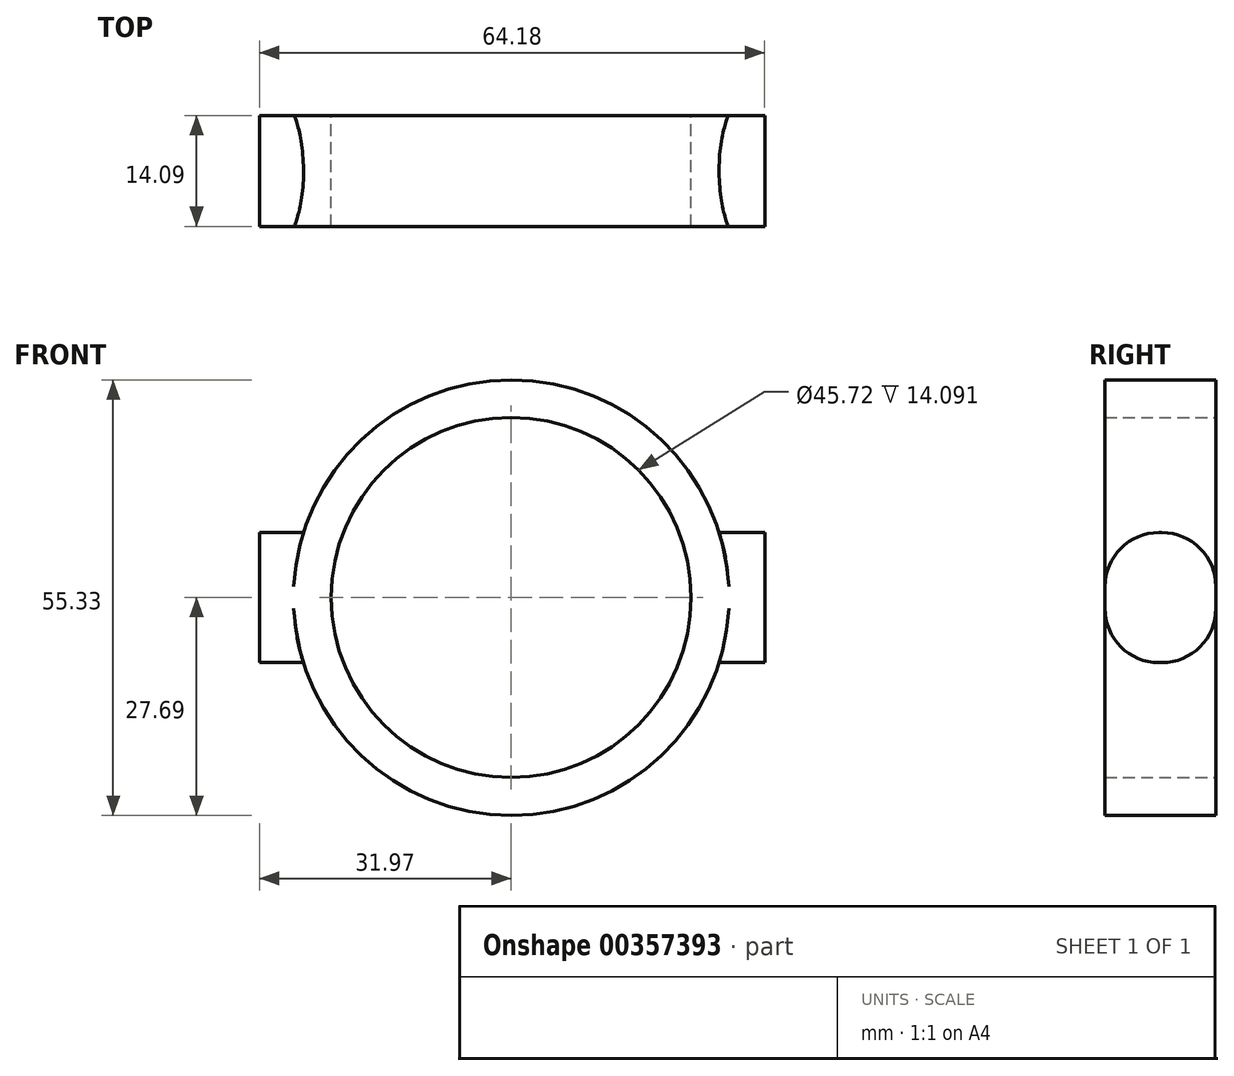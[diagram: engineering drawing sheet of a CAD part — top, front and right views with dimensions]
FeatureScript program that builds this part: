
annotation { "Feature Type Name" : "Feature", "Feature Type Description" : "" }
export const myFeature = defineFeature(function(context is Context, id is Id, definition is map)
    precondition{}
    {
        {
            var Q0;
            Q0=qCreatedBy(makeId("Front.planeOp"),FACE);
            var sketch = newSketch(context, id + "F0", { "sketchPlane" : qUnion([Q0])});
            skCircle(sketch, "E0", {"center": v(0.02, -0.03) * mm, "radius": 27.66 * mm});
            skPoint(sketch, "E0.first.point", {"position": v(27.68, 0) * mm});
            skPoint(sketch, "E0.second.point", {"position": v(-27.65, 0) * mm});
            skPoint(sketch, "E0.third.point", {"position": v(0, -27.7) * mm});
            skLineSegment(sketch, "E1", {"start": v(32.21, 8.25) * mm, "end": v(-31.97, 8.25) * mm});
            skLineSegment(sketch, "E2", {"start": v(-31.97, -8.28) * mm, "end": v(32.21, -8.28) * mm});
            skLineSegment(sketch, "E3", {"start": v(-31.97, 8.25) * mm, "end": v(-31.97, -8.28) * mm});
            skLineSegment(sketch, "E4", {"start": v(32.21, 8.25) * mm, "end": v(32.21, -8.28) * mm});
            skSolve(sketch);
        }
        {
            var Q0;
            Q0=qSketchRegion(id+"F0",true);
            var Q1;
            Q1=sQuery(id+"F0.wireOp",EDGE,"E0");
            var Q2;
            Q2=sQuery(id+"F0.wireOp",EDGE,"E2");
            var Q3;
            Q3=sQuery(id+"F0.wireOp",EDGE,"E1");
            var Q4;
            Q4=sQuery(id+"F0.wireOp",EDGE,"E3");
            var Q5;
            Q5=sQuery(id+"F0.wireOp",EDGE,"E4");
            extrude(context, id + "F1", {"entities" : qUnion([Q0]), "surfaceEntities" : qUnion([Q1, Q2, Q3, Q4, Q5]), "depth" : 14.1 * mm});
        }
        {
            var Q0;
            Q0=qCreatedBy(makeId("Front.planeOp"),FACE);
            var sketch = newSketch(context, id + "F2", { "sketchPlane" : qUnion([Q0])});
            skPoint(sketch, "E5", {"position": v(0, 0) * mm});
            skSolve(sketch);
        }
        {
            var Q0;
            Q0=sQuery(id+"F2.wireOp",VERTEX,"E5");
            var Q1;
            Q1=makeQuery(id+"F1.opExtrude","SWEPT_BODY",BODY,{"disambiguationData":[OSD([sQuery(id+"F0.wireOp",EDGE,"E0"),sQuery(id+"F0.wireOp",EDGE,"E1"),sQuery(id+"F0.wireOp",EDGE,"E2"),sQuery(id+"F0.wireOp",EDGE,"E3"),sQuery(id+"F0.wireOp",EDGE,"E4")])]});
            hole(context, id + "F3", {"style" : HoleStyle.SIMPLE, "endStyle" : HoleEndStyle.THROUGH, "oppositeDirection" : true, "holeDiameter" : 45.72 * mm, "isTappedThrough" : true, "tappedDepth" : 12.7 * mm, "tapClearance" : 3, "locations" : qUnion([Q0]), "scope" : qUnion([Q1])});
        }
        {
            var Q0;
            {var subQ0=sQuery(id+"F0.wireOp",EDGE,"E2");Q0=makeQuery(id+"F1.opExtrude","CAP_EDGE",EDGE,{"disambiguationData":[OSD([subQ0]),TDD([makeQuery(id+"F0.imprint","IMPRINT",EDGE,{"disambiguationData":[TD([[makeQuery(id+"F0.imprint","INTERSECT",VERTEX,{"derivedFrom":[subQ0,sQuery(id+"F0.wireOp",EDGE,"E4")]}),1.0]])],"derivedFrom":subQ0})])],"isStart":false});}
            var Q1;
            {var subQ0=sQuery(id+"F0.wireOp",EDGE,"E2");Q1=makeQuery(id+"F1.opExtrude","CAP_EDGE",EDGE,{"disambiguationData":[OSD([subQ0]),TDD([makeQuery(id+"F0.imprint","IMPRINT",EDGE,{"disambiguationData":[TD([[makeQuery(id+"F0.imprint","INTERSECT",VERTEX,{"derivedFrom":[subQ0,sQuery(id+"F0.wireOp",EDGE,"E4")]}),1.0]])],"derivedFrom":subQ0})])],"isStart":true});}
            var Q2;
            {var subQ0=sQuery(id+"F0.wireOp",EDGE,"E1");Q2=makeQuery(id+"F1.opExtrude","CAP_EDGE",EDGE,{"disambiguationData":[OSD([subQ0]),TDD([makeQuery(id+"F0.imprint","IMPRINT",EDGE,{"disambiguationData":[TD([[makeQuery(id+"F0.imprint","INTERSECT",VERTEX,{"derivedFrom":[subQ0,sQuery(id+"F0.wireOp",EDGE,"E4")]}),-1.0]])],"derivedFrom":subQ0})])],"isStart":false});}
            var Q3;
            {var subQ0=sQuery(id+"F0.wireOp",EDGE,"E1");Q3=makeQuery(id+"F1.opExtrude","CAP_EDGE",EDGE,{"disambiguationData":[OSD([subQ0]),TDD([makeQuery(id+"F0.imprint","IMPRINT",EDGE,{"disambiguationData":[TD([[makeQuery(id+"F0.imprint","INTERSECT",VERTEX,{"derivedFrom":[subQ0,sQuery(id+"F0.wireOp",EDGE,"E4")]}),-1.0]])],"derivedFrom":subQ0})])],"isStart":true});}
            fillet(context, id + "F4", {"entities" : qUnion([Q0, Q1, Q2, Q3]), "radius" : 6.86 * mm, "tangentPropagation" : true, "allowEdgeOverflow" : false});
        }
        {
            var Q0;
            {var subQ0=sQuery(id+"F0.wireOp",EDGE,"E2");Q0=makeQuery(id+"F1.opExtrude","CAP_EDGE",EDGE,{"disambiguationData":[OSD([subQ0]),TDD([makeQuery(id+"F0.imprint","IMPRINT",EDGE,{"disambiguationData":[TD([[makeQuery(id+"F0.imprint","INTERSECT",VERTEX,{"derivedFrom":[subQ0,sQuery(id+"F0.wireOp",EDGE,"E3")]}),-1.0]])],"derivedFrom":subQ0})])],"isStart":false});}
            var Q1;
            {var subQ0=sQuery(id+"F0.wireOp",EDGE,"E1");Q1=makeQuery(id+"F1.opExtrude","CAP_EDGE",EDGE,{"disambiguationData":[OSD([subQ0]),TDD([makeQuery(id+"F0.imprint","IMPRINT",EDGE,{"disambiguationData":[TD([[makeQuery(id+"F0.imprint","INTERSECT",VERTEX,{"derivedFrom":[subQ0,sQuery(id+"F0.wireOp",EDGE,"E3")]}),1.0]])],"derivedFrom":subQ0})])],"isStart":false});}
            var Q2;
            {var subQ0=sQuery(id+"F0.wireOp",EDGE,"E1");Q2=makeQuery(id+"F1.opExtrude","CAP_EDGE",EDGE,{"disambiguationData":[OSD([subQ0]),TDD([makeQuery(id+"F0.imprint","IMPRINT",EDGE,{"disambiguationData":[TD([[makeQuery(id+"F0.imprint","INTERSECT",VERTEX,{"derivedFrom":[subQ0,sQuery(id+"F0.wireOp",EDGE,"E3")]}),1.0]])],"derivedFrom":subQ0})])],"isStart":true});}
            var Q3;
            {var subQ0=sQuery(id+"F0.wireOp",EDGE,"E2");Q3=makeQuery(id+"F1.opExtrude","CAP_EDGE",EDGE,{"disambiguationData":[OSD([subQ0]),TDD([makeQuery(id+"F0.imprint","IMPRINT",EDGE,{"disambiguationData":[TD([[makeQuery(id+"F0.imprint","INTERSECT",VERTEX,{"derivedFrom":[subQ0,sQuery(id+"F0.wireOp",EDGE,"E3")]}),-1.0]])],"derivedFrom":subQ0})])],"isStart":true});}
            fillet(context, id + "F5", {"entities" : qUnion([Q0, Q1, Q2, Q3]), "radius" : 6.86 * mm, "tangentPropagation" : true, "allowEdgeOverflow" : false});
        }
    });
